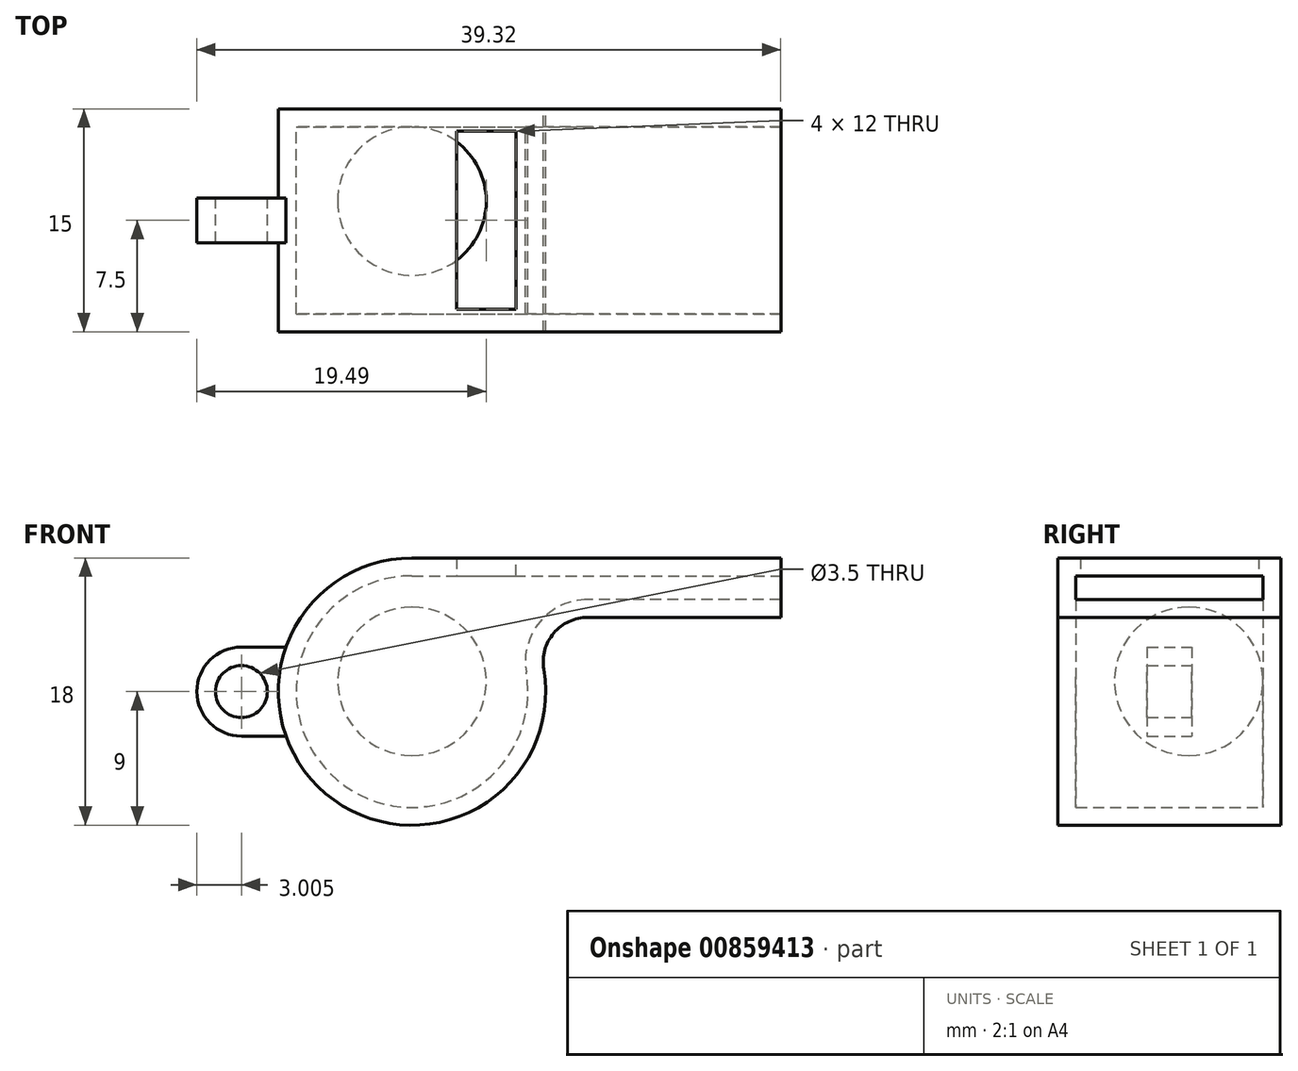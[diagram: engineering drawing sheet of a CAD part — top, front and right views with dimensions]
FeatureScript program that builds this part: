
annotation { "Feature Type Name" : "Feature", "Feature Type Description" : "" }
export const myFeature = defineFeature(function(context is Context, id is Id, definition is map)
    precondition{}
    {
        {
            var Q0;
            Q0=qCreatedBy(makeId("Front.planeOp"),FACE);
            var sketch = newSketch(context, id + "F0", { "sketchPlane" : qUnion([Q0])});
            skArc(sketch, "E0", {"start": v(0, 9) * mm, "mid": v(-5.8, -6.87) * mm, "end": v(8.87, 1.5) * mm});
            skLineSegment(sketch, "E1", {"start": v(0, 9) * mm, "end": v(24.83, 9) * mm});
            skLineSegment(sketch, "E2", {"start": v(24.83, 5) * mm, "end": v(11.83, 5) * mm});
            skPoint(sketch, "E3.visualSharp", {"position": v(7.48, 5) * mm});
            skArc(sketch, "E3.filletArc", {"start": v(11.83, 5) * mm, "mid": v(9.54, 3.94) * mm, "end": v(8.87, 1.5) * mm});
            skLineSegment(sketch, "E4", {"start": v(24.83, 9) * mm, "end": v(24.83, 5) * mm});
            skSolve(sketch);
        }
        {
            var Q0;
            Q0=qSketchRegion(id+"F0",true);
            extrude(context, id + "F1", {"entities" : qUnion([Q0]), "endBound" : BoundingType.SYMMETRIC, "depth" : 15 * mm, "offsetDistance" : 25 * mm});
        }
        {
            var Q0;
            Q0=makeQuery(id+"F1.opExtrude","SWEPT_FACE",FACE,{"disambiguationData":[OSD([sQuery(id+"F0.wireOp",EDGE,"E4")])]});
            shell(context, id + "F2", {"entities" : qUnion([Q0]), "thickness" : 1.2 * mm});
        }
        {
            var Q0;
            Q0=qCreatedBy(makeId("Front.planeOp"),FACE);
            var sketch = newSketch(context, id + "F3", { "sketchPlane" : qUnion([Q0])});
            skLineSegment(sketch, "E5", {"start": v(3, 9) * mm, "end": v(3, 7.8) * mm});
            skLineSegment(sketch, "E6", {"start": v(3, 7.8) * mm, "end": v(7, 7.8) * mm});
            skLineSegment(sketch, "E7", {"start": v(7, 7.8) * mm, "end": v(7, 9) * mm});
            skLineSegment(sketch, "E8", {"start": v(3, 9) * mm, "end": v(7, 9) * mm});
            skSolve(sketch);
        }
        {
            var Q0;
            Q0=qSketchRegion(id+"F3",true);
            extrude(context, id + "F4", {"entities" : qUnion([Q0]), "operationType" : NewBodyOperationType.REMOVE, "endBound" : BoundingType.SYMMETRIC, "oppositeDirection" : true, "depth" : 12 * mm, "offsetDistance" : 25 * mm});
        }
        {
            var Q0;
            Q0=qCreatedBy(makeId("Front.planeOp"),FACE);
            var sketch = newSketch(context, id + "F5", { "sketchPlane" : qUnion([Q0])});
            skCircle(sketch, "E9", {"center": v(-11.49, 0) * mm, "radius": 1.75 * mm});
            skArc(sketch, "E10", {"start": v(-11.49, 3) * mm, "mid": v(-14.49, 0) * mm, "end": v(-11.49, -3) * mm});
            skLineSegment(sketch, "E11", {"start": v(-11.49, 3) * mm, "end": v(-8.49, 3) * mm});
            skLineSegment(sketch, "E12", {"start": v(-8.49, 3) * mm, "end": v(-8.49, -3) * mm});
            skLineSegment(sketch, "E13", {"start": v(-8.49, -3) * mm, "end": v(-11.49, -3) * mm});
            skSolve(sketch);
        }
        {
            var Q0;
            Q0=qSketchRegion(id+"F5",true);
            extrude(context, id + "F6", {"entities" : qUnion([Q0]), "operationType" : NewBodyOperationType.ADD, "endBound" : BoundingType.SYMMETRIC, "depth" : 3 * mm, "offsetDistance" : 25 * mm});
        }
        {
            var Q0;
            Q0=qCreatedBy(makeId("Front.planeOp"),FACE);
            var sketch = newSketch(context, id + "F7", { "sketchPlane" : qUnion([Q0])});
            skArc(sketch, "E14", {"start": v(0, -7.8) * mm, "mid": v(5, -2.8) * mm, "end": v(0, 2.2) * mm});
            skLineSegment(sketch, "E15", {"start": v(0, 2.2) * mm, "end": v(0, -7.8) * mm});
            skSolve(sketch);
        }
        {
            var Q0;
            Q0=qSketchRegion(id+"F7",true);
            var Q1;
            Q1=sQuery(id+"F7.wireOp",EDGE,"E15");
            var Q2;
            Q2=sQuery(id+"F7.wireOp",EDGE,"E14");
            var Q3;
            Q3=sQuery(id+"F7.wireOp",EDGE,"E15");
            revolve(context, id + "F8", {"surfaceOperationType" : NewSurfaceOperationType.NEW, "entities" : qUnion([Q0]), "surfaceEntities" : qUnion([Q1, Q2]), "axis" : qUnion([Q3]), "revolveType" : RevolveType.FULL});
        }
        {
            var Q0;
            Q0=makeQuery(id+"F8.opRevolve","SWEPT_BODY",BODY,{"disambiguationData":[OSD([sQuery(id+"F7.wireOp",EDGE,"E14"),sQuery(id+"F7.wireOp",EDGE,"E15")])]});
            var Q1;
            {var subQ0=sQuery(id+"F0.wireOp",EDGE,"E3.filletArc");var subQ1=sQuery(id+"F0.wireOp",EDGE,"E2");var subQ2=sQuery(id+"F0.wireOp",EDGE,"MtSjJYmz-mpyd-ET7v-4B5w-YfVtobTtKdcY");var subQ3=sQuery(id+"F0.wireOp",EDGE,"qCv6GezB-KdKX-WKvb-SZfC-B69hnCbk2Tn7");var subQ4=sQuery(id+"F0.wireOp",EDGE,"6amGEErQ-mQCb-uGRf-FdpP-mwo6pWPg8KFU");var subQ5=sQuery(id+"F0.wireOp",EDGE,"FKTEPIuX-czqb-elMn-F3ep-rWvDLRjA0JRG");var subQ6=sQuery(id+"F0.wireOp",EDGE,"S7LQD6k4-7zi6-8QOl-ic7p-YOfLqTzotLk0");var subQ7=sQuery(id+"F0.wireOp",EDGE,"E1");var subQ8=sQuery(id+"F0.wireOp",EDGE,"E0");Q1=makeQuery(id+"F2.opShell","OFFSET_FACE",FACE,{"disambiguationData":[OSD([subQ8,subQ7,subQ6,subQ5,subQ4,subQ3,subQ2,subQ1,subQ0]),TDD([makeQuery(id+"F1.opExtrude","CAP_FACE",FACE,{"disambiguationData":[OSD([subQ8,subQ7,subQ6,subQ5,subQ4,subQ3,subQ2,subQ1,subQ0])],"isStart":true})])]});}
            transform(context, id + "F9", {"entities" : qUnion([Q0]), "transformType" : TransformType.TRANSLATION_3D, "dx" : 0 * mm, "dy" : 1.3 * mm, "dz" : 3.5 * mm, "makeCopy" : false});
        }
    });
